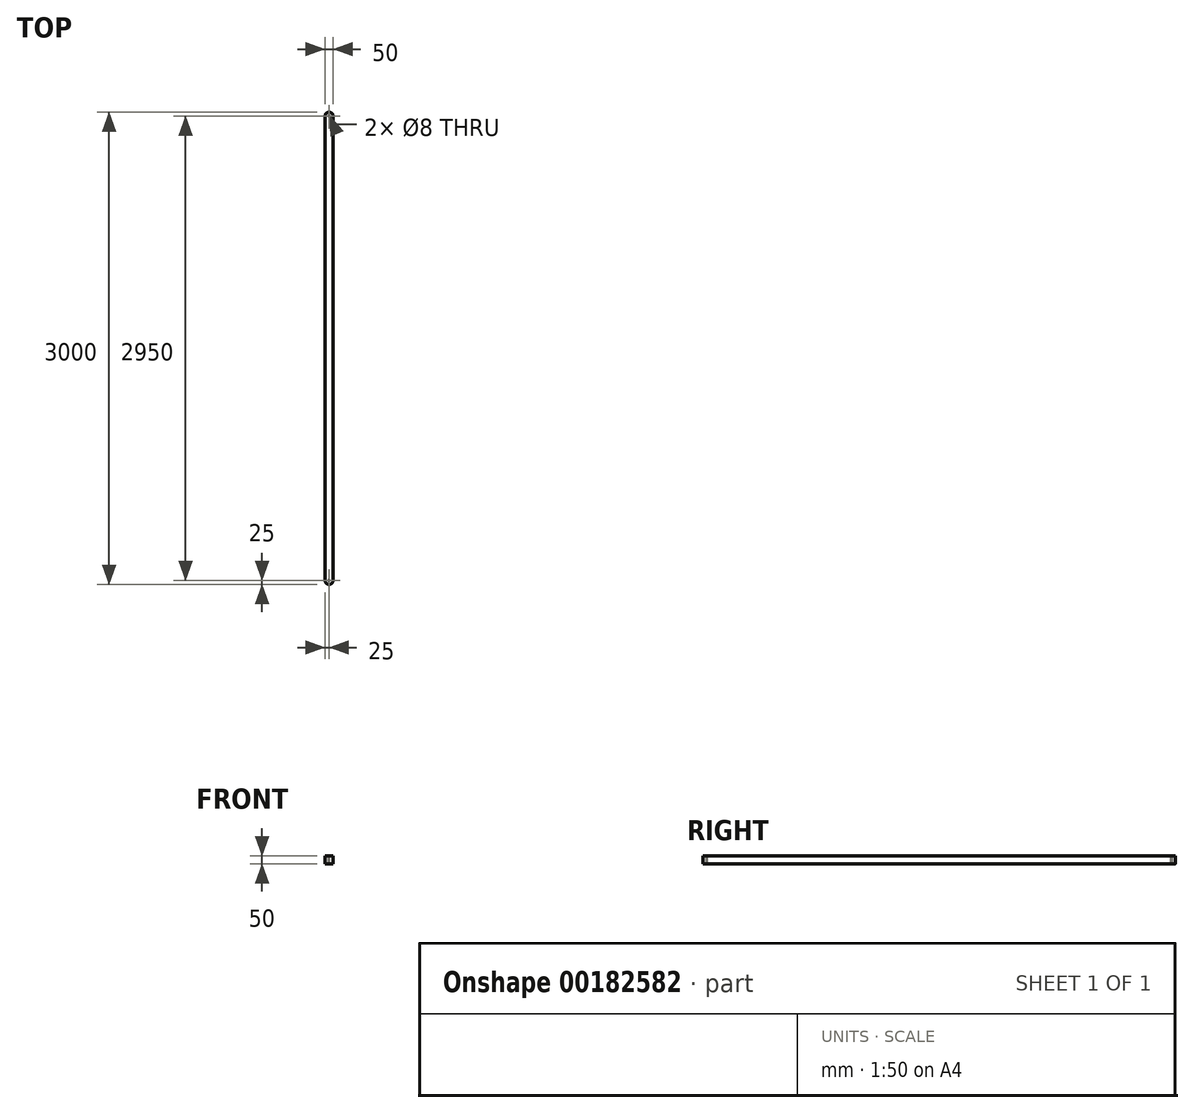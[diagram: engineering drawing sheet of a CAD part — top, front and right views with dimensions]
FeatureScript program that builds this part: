
annotation { "Feature Type Name" : "Feature", "Feature Type Description" : "" }
export const myFeature = defineFeature(function(context is Context, id is Id, definition is map)
    precondition{}
    {
        {
            var Q0;
            Q0=qCreatedBy(makeId("Front.planeOp"),FACE);
            var sketch = newSketch(context, id + "F0", { "sketchPlane" : qUnion([Q0])});
            skLineSegment(sketch, "E0.bottom", {"start": v(0, 0) * mm, "end": v(50, 0) * mm});
            skLineSegment(sketch, "E0.top", {"start": v(0, 50) * mm, "end": v(50, 50) * mm});
            skLineSegment(sketch, "E0.left", {"start": v(0, 0) * mm, "end": v(0, 50) * mm});
            skLineSegment(sketch, "E0.right", {"start": v(50, 0) * mm, "end": v(50, 50) * mm});
            skSolve(sketch);
        }
        {
            var Q0;
            Q0=makeQuery(id+"F0.imprint","IMPRINT",FACE,{"disambiguationData":[TD([[makeQuery(id+"F0.imprint","IMPRINT",EDGE,{"derivedFrom":sQuery(id+"F0.wireOp",EDGE,"E0.bottom")}),1.0]])]});
            extrude(context, id + "F1", {"entities" : qUnion([Q0]), "depth" : 3000 * mm});
        }
        {
            var Q0;
            Q0=makeQuery(id+"F1.opExtrude","SWEPT_FACE",FACE,{"disambiguationData":[OSD([sQuery(id+"F0.wireOp",EDGE,"E0.top")])]});
            var sketch = newSketch(context, id + "F2", { "sketchPlane" : qUnion([Q0])});
            skPoint(sketch, "E1.endSnap0", {"position": v(25, 0) * mm});
            skCircle(sketch, "E2", {"center": v(25, -25) * mm, "radius": 4 * mm});
            skCircle(sketch, "E3", {"center": v(25, -2975) * mm, "radius": 4 * mm});
            skSolve(sketch);
        }
        {
            var Q0;
            Q0=qSketchRegion(id+"F2",true);
            extrude(context, id + "F3", {"entities" : qUnion([Q0]), "operationType" : NewBodyOperationType.REMOVE, "endBound" : BoundingType.THROUGH_ALL, "oppositeDirection" : true, "depth" : 25 * mm});
        }
        {
            var Q0;
            Q0=makeQuery(id+"F1.opExtrude","SWEPT_FACE",FACE,{"disambiguationData":[OSD([sQuery(id+"F0.wireOp",EDGE,"E0.top")])]});
            var sketch = newSketch(context, id + "F4", { "sketchPlane" : qUnion([Q0])});
            skArc(sketch, "E4", {"start": v(50, -25) * mm, "mid": v(25, 0) * mm, "end": v(0, -25) * mm});
            skArc(sketch, "E5", {"start": v(0, -2975) * mm, "mid": v(25, -3000) * mm, "end": v(50, -2975) * mm});
            skLineSegment(sketch, "E6.top", {"start": v(50, -3000) * mm, "end": v(0, -3000) * mm});
            skLineSegment(sketch, "E6.left", {"start": v(50, -2975) * mm, "end": v(50, -3000) * mm});
            skLineSegment(sketch, "E6.right", {"start": v(0, -2975) * mm, "end": v(0, -3000) * mm});
            skLineSegment(sketch, "E7.top", {"start": v(0, 0) * mm, "end": v(50, 0) * mm});
            skLineSegment(sketch, "E7.left", {"start": v(0, -25) * mm, "end": v(0, 0) * mm});
            skLineSegment(sketch, "E7.right", {"start": v(50, -25) * mm, "end": v(50, 0) * mm});
            skSolve(sketch);
        }
        {
            var Q0;
            Q0=qSketchRegion(id+"F4",true);
            extrude(context, id + "F5", {"entities" : qUnion([Q0]), "operationType" : NewBodyOperationType.REMOVE, "endBound" : BoundingType.UP_TO_NEXT, "oppositeDirection" : true, "depth" : 25 * mm});
        }
    });
